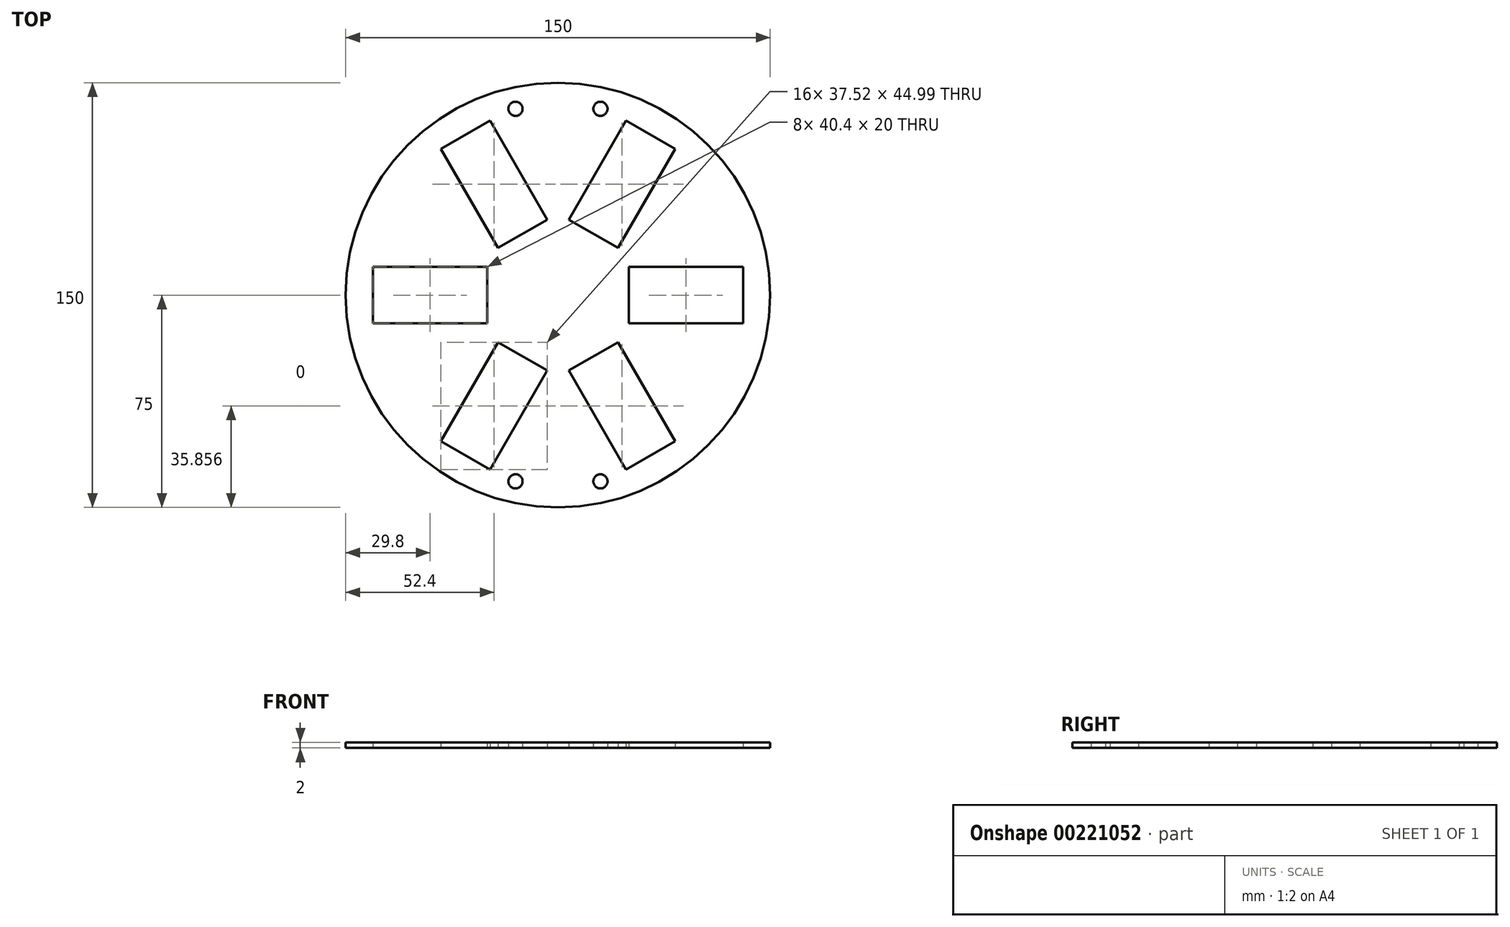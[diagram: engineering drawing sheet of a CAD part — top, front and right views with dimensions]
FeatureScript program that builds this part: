
annotation { "Feature Type Name" : "Feature", "Feature Type Description" : "" }
export const myFeature = defineFeature(function(context is Context, id is Id, definition is map)
    precondition{}
    {
        {
            var Q0;
            Q0=qCreatedBy(makeId("Top.planeOp"),FACE);
            var sketch = newSketch(context, id + "F0", { "sketchPlane" : qUnion([Q0])});
            skCircle(sketch, "E0", {"center": v(0, 0) * mm, "radius": 75 * mm});
            skLineSegment(sketch, "E1.bottom", {"start": v(-65.4, 10) * mm, "end": v(-25, 10) * mm});
            skLineSegment(sketch, "E1.top", {"start": v(-65.4, -10) * mm, "end": v(-25, -10) * mm});
            skLineSegment(sketch, "E1.left", {"start": v(-65.4, 10) * mm, "end": v(-65.4, -10) * mm});
            skLineSegment(sketch, "E1.right", {"start": v(-25, 10) * mm, "end": v(-25, -10) * mm});
            skLineSegment(sketch, "E2.1.0", {"start": v(-21.16, -16.65) * mm, "end": v(-3.84, -26.65) * mm});
            skLineSegment(sketch, "E2.1.1", {"start": v(-41.36, -51.64) * mm, "end": v(-21.16, -16.65) * mm});
            skLineSegment(sketch, "E2.1.2", {"start": v(-41.36, -51.64) * mm, "end": v(-24.04, -61.64) * mm});
            skLineSegment(sketch, "E2.1.3", {"start": v(-24.04, -61.64) * mm, "end": v(-3.84, -26.65) * mm});
            skLineSegment(sketch, "E2.2.0", {"start": v(3.84, -26.65) * mm, "end": v(21.16, -16.65) * mm});
            skLineSegment(sketch, "E2.2.1", {"start": v(24.04, -61.64) * mm, "end": v(3.84, -26.65) * mm});
            skLineSegment(sketch, "E2.2.2", {"start": v(24.04, -61.64) * mm, "end": v(41.36, -51.64) * mm});
            skLineSegment(sketch, "E2.2.3", {"start": v(41.36, -51.64) * mm, "end": v(21.16, -16.65) * mm});
            skLineSegment(sketch, "E2.3.0", {"start": v(25, -10) * mm, "end": v(25, 10) * mm});
            skLineSegment(sketch, "E2.3.1", {"start": v(65.4, -10) * mm, "end": v(25, -10) * mm});
            skLineSegment(sketch, "E2.3.2", {"start": v(65.4, -10) * mm, "end": v(65.4, 10) * mm});
            skLineSegment(sketch, "E2.3.3", {"start": v(65.4, 10) * mm, "end": v(25, 10) * mm});
            skLineSegment(sketch, "E2.4.0", {"start": v(21.16, 16.65) * mm, "end": v(3.84, 26.65) * mm});
            skLineSegment(sketch, "E2.4.1", {"start": v(41.36, 51.64) * mm, "end": v(21.16, 16.65) * mm});
            skLineSegment(sketch, "E2.4.2", {"start": v(41.36, 51.64) * mm, "end": v(24.04, 61.64) * mm});
            skLineSegment(sketch, "E2.4.3", {"start": v(24.04, 61.64) * mm, "end": v(3.84, 26.65) * mm});
            skLineSegment(sketch, "E2.5.0", {"start": v(-3.84, 26.65) * mm, "end": v(-21.16, 16.65) * mm});
            skLineSegment(sketch, "E2.5.1", {"start": v(-24.04, 61.64) * mm, "end": v(-3.84, 26.65) * mm});
            skLineSegment(sketch, "E2.5.2", {"start": v(-24.04, 61.64) * mm, "end": v(-41.36, 51.64) * mm});
            skLineSegment(sketch, "E2.5.3", {"start": v(-41.36, 51.64) * mm, "end": v(-21.16, 16.65) * mm});
            skCircle(sketch, "E3", {"center": v(15, 65.81) * mm, "radius": 2.5 * mm});
            skCircle(sketch, "E4.1.0", {"center": v(-15, -65.81) * mm, "radius": 2.5 * mm});
            skLineSegment(sketch, "E4.anchor1", {"start": v(0, 0) * mm, "end": v(15, 65.81) * mm, "construction": true});
            skLineSegment(sketch, "E4.anchor2", {"start": v(0, 0) * mm, "end": v(-15, -65.81) * mm, "construction": true});
            skCircle(sketch, "E5.MirrorC", {"center": v(15, -65.81) * mm, "radius": 2.5 * mm});
            skCircle(sketch, "E6.MirrorC", {"center": v(-15, 65.81) * mm, "radius": 2.5 * mm});
            skSolve(sketch);
        }
        {
            var Q0;
            Q0=makeQuery(id+"F0.imprint","IMPRINT",FACE,{"disambiguationData":[TD([[makeQuery(id+"F0.imprint","IMPRINT",EDGE,{"derivedFrom":sQuery(id+"F0.wireOp",EDGE,"E0")}),1.0]])]});
            extrude(context, id + "F1", {"entities" : qUnion([Q0]), "depth" : 2 * mm});
        }
    });
